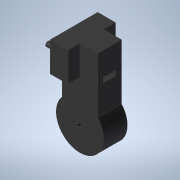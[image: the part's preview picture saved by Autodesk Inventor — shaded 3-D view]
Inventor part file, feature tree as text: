
AUTODESK INVENTOR PART (.ipt)
format: ipt  version: 2022 (Build 260153000, 153)  size: 278,528 bytes
history: native  units: in
note: dims shown in document units (in); Inventor stores cm internally (conversion verified against a paired STEP export)
features: extrude x18, sketch x18, chamfer x1
ambient origin geometry x8: Origin, YZ Plane, XZ Plane, XY Plane, X Axis, Y Axis, Z Axis, Center Point
bodies: Solid1 (feature_tree)
feature tree (37):
  extrude  "Extrusion1"  Depth=1.5748in
  extrude  "Extrusion2"  Depth=1.1811in
  extrude  "Extrusion3"  Depth=0.7874in
  extrude  "Extrusion4"  Depth=0.2362in
  extrude  "Extrusion5"  Depth=0.2362in
  extrude  "Extrusion6"  Depth=0.9055in TaperAngle=0.0deg
  extrude  "Extrusion7"  Depth=0.189in
  extrude  "Extrusion8"  Depth=0.6299in TaperAngle=0.0deg
  sketch  "Sketch11"  dims[d24=0.0984in d25=0.0591in]
  extrude  "Extrusion9"  Depth=0.0591in
  extrude  "Extrusion10"  Depth=0.0591in
  extrude  "Extrusion11"  Depth=0.3937in
  extrude  "Extrusion12"  Depth=0.1969in
  extrude  "Extrusion13"  Depth=0.1969in TaperAngle=0.0deg
  extrude  "Extrusion14"  Depth=0.0787in
  extrude  "Extrusion15"  Depth=0.1181in
  extrude  "Extrusion16"  Depth=0.3937in TaperAngle=0.0deg
  extrude  "Extrusion17"  Depth=0.3937in
  extrude  "Extrusion18"  Depth=0.3937in TaperAngle=0.0deg
  chamfer  "Chamfer2"  Distance=0.3937in
  sketch  "Sketch1"  dims[d0=0.7874in d1=1.5748in]
  sketch  "Sketch2"  dims[d2=1.1811in d3=1.9685in]
  sketch  "Sketch4"  dims[d4=0.7874in d5=0.0in d6=0.7874in]
  sketch  "Sketch6"  dims[d7=0.5906in d8=0.0in d13=0.2362in]
  sketch  "Sketch7"  dims[d14=0.9843in d15=0.2362in]
  sketch  "Sketch8"  dims[d16=0.9055in d17=0.9055in d18=0.0in]
  sketch  "Sketch9"  dims[d19=0.4724in d20=0.189in]
  sketch  "Sketch10"  dims[d21=0.189in d22=0.6299in d23=0.0in]
  sketch  "Sketch12"  dims[d26=0.0984in d27=0.0591in]
  sketch  "Sketch13"  dims[d28=0.315in d29=0.0in d30=0.3937in]
  sketch  "Sketch15"  dims[d31=0.315in d32=0.1969in]
  sketch  "Sketch16"  dims[d33=0.1969in d34=0.6225in d35=0.0in]
  sketch  "Sketch17"  dims[d36=0.0787in d37=0.1181in]
  sketch  "Sketch18"  dims[d38=0.1181in d39=0.1181in]
  sketch  "Sketch19"  dims[d40=0.315in d41=0.0in d45=0.3937in d46=0.0in]
  sketch  "Sketch20"  dims[d47=0.5906in d48=0.3937in]
  sketch  "Sketch21"  dims[d49=2.3469in d50=0.0in d51=0.3937in d52=0.0in d53=0.3937in d54=0.0in d56=0.9843in d57=0.3937in d58=0.0in d59=0.3937in d60=0.0in d61=0.9173in d62=0.7874in d63=0.3937in d64=0.2362in d65=0.1575in d66=0.2362in d67=0.1575in d68=0.315in d69=0.0in d70=0.6299in d71=0.0in d72=0.7874in d73=0.6299in d74=0.0in d75=1.1826in d76=0.0in d77=0.0787in d78=0.0787in d79=5.4424in d80=0.0in d81=0.315in d82=0.0787in d83=45.0deg]
